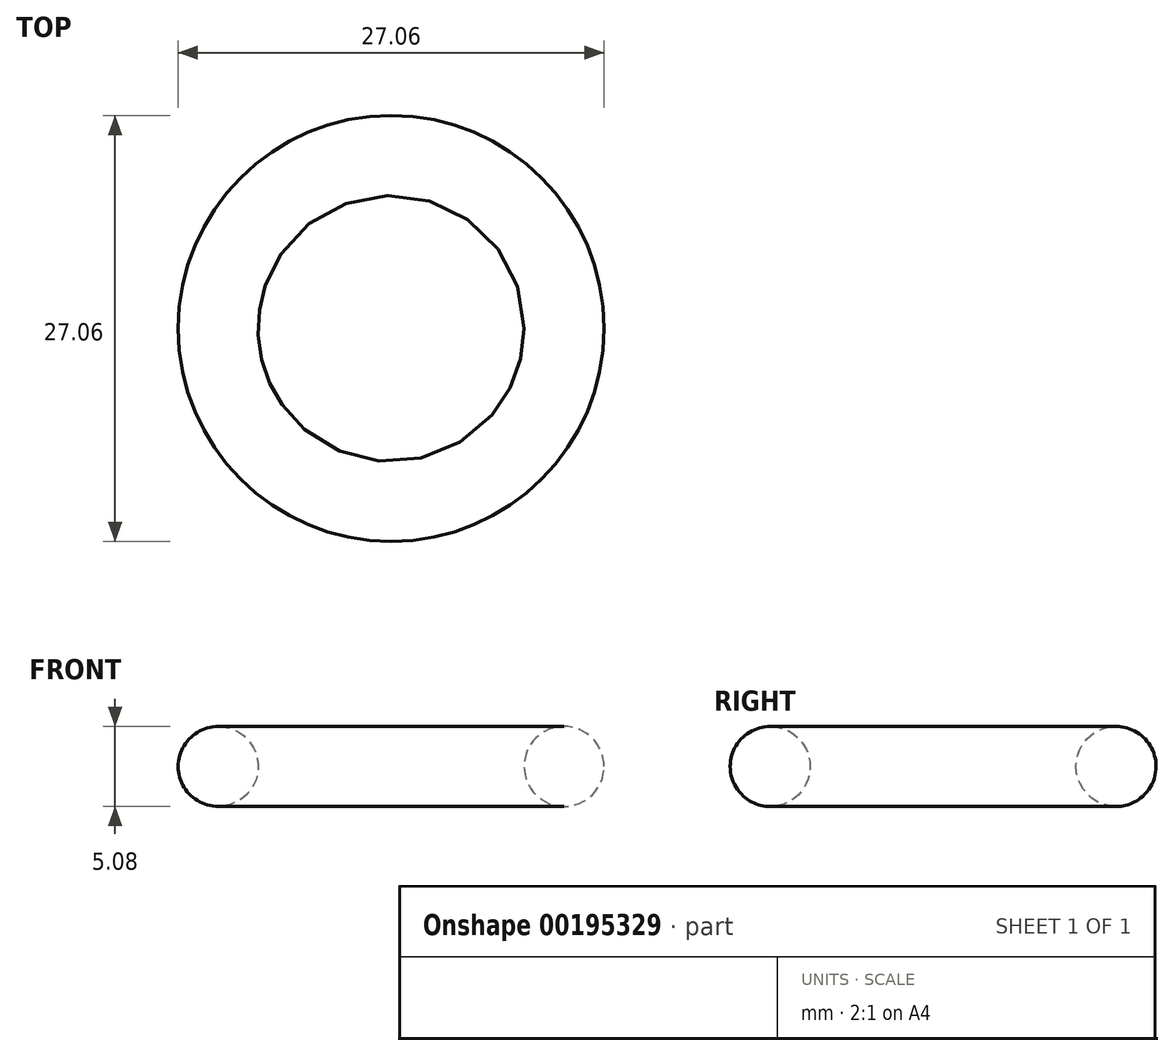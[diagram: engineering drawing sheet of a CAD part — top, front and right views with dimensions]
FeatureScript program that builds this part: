
annotation { "Feature Type Name" : "Feature", "Feature Type Description" : "" }
export const myFeature = defineFeature(function(context is Context, id is Id, definition is map)
    precondition{}
    {
        {
            var Q0;
            Q0=qCreatedBy(makeId("Front.planeOp"),FACE);
            var sketch = newSketch(context, id + "F0", { "sketchPlane" : qUnion([Q0])});
            skLineSegment(sketch, "E0", {"start": v(0, 12.7) * mm, "end": v(0, 0) * mm});
            skCircle(sketch, "E1", {"center": v(10.99, 0) * mm, "radius": 2.54 * mm});
            skSolve(sketch);
        }
        {
            var Q0;
            Q0=makeQuery(id+"F0.imprint","IMPRINT",FACE,{"disambiguationData":[TD([[makeQuery(id+"F0.imprint","IMPRINT",EDGE,{"derivedFrom":sQuery(id+"F0.wireOp",EDGE,"E1")}),1.0]])]});
            var Q1;
            Q1=sQuery(id+"F0.wireOp",EDGE,"E0");
            revolve(context, id + "F1", {"entities" : qUnion([Q0]), "axis" : qUnion([Q1]), "revolveType" : RevolveType.FULL});
        }
    });
